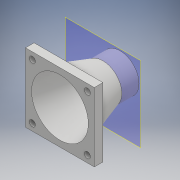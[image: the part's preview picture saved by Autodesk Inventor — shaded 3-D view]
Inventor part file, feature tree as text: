
AUTODESK INVENTOR PART (.ipt)
format: ipt  version: 2018 (Build 220112000, 112)  size: 156,672 bytes
history: native  units: mm
features: sketch x6, hole x4, extrude x2, loft x2, plane x1
ambient origin geometry x8: Origin, YZ Plane, XZ Plane, XY Plane, X Axis, Y Axis, Z Axis, Center Point
bodies: Solid1 (feature_tree)
feature tree (15):
  extrude  "Extrusion1"  Depth=40.0mm
  sketch  "Sketch2"  dims[d2=5.0mm d3=0.0mm d4=35.0mm]
  plane  "Work Plane1"
  loft  "Loft1"
  loft  "Loft2"
  extrude  "Extrusion3"  TaperAngle=0.0deg  [1 undecoded]
  hole  "Hole1"  [1 undecoded]
  hole  "Hole2"  [1 undecoded]
  hole  "Hole3"  [1 undecoded]
  hole  "Hole4"  [1 undecoded]
  sketch  "Sketch1"  dims[d0=40.0mm d1=40.0mm]
  sketch  "Sketch3"  dims[d5=20.0mm d6=22.0mm]
  sketch  "Sketch6"  dims[d7=0.0mm d8=90.0deg d9=0.0mm d10=90.0deg]
  sketch  "Sketch8"  dims[d15=18.0mm d16=33.0mm]
  sketch  "Sketch9"  dims[d17=0.0mm d18=90.0deg d19=0.0mm d20=90.0deg d21=22.0mm d22=18.0mm d23=10.0mm d24=0.0mm d25=4.0mm d26=4.0mm d27=3.5mm d28=6.0mm d29=4.0mm d30=2.0mm d31=90.0deg d32=8.0mm d33=20.594885mm d34=4.0mm d35=4.0mm d36=3.5mm d37=6.0mm d38=4.0mm d39=2.0mm d40=90.0deg d41=8.0mm d42=20.594885mm d43=4.0mm d44=4.0mm d45=3.5mm d46=6.0mm d47=4.0mm d48=2.0mm d49=90.0deg d50=8.0mm d51=20.594885mm d52=4.0mm d53=4.0mm d54=3.5mm d55=6.0mm d56=4.0mm d57=2.0mm d58=90.0deg d59=8.0mm d60=20.594885mm]
note: 5 required parameter values undecoded (feature->parameter linkage not recoverable at this tier; creation-order binding heuristic only, values carry confidence <= 0.55)
